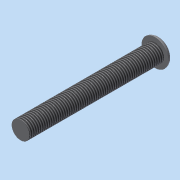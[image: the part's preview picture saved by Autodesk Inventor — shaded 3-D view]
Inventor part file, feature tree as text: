
AUTODESK INVENTOR PART (.ipt)
format: ipt  version: 2015 (Build 190159000, 159)  size: 94,208 bytes
history: native  units: mm
features: revolve x1, fillet x1, thread x1, sketch x1
ambient origin geometry x8: Origin, YZ Plane, XZ Plane, XY Plane, X Axis, Y Axis, Z Axis, Center Point
bodies: Solid1 (feature_tree)
feature tree (4):
  revolve  "Revolution1"  [1 undecoded]
  fillet  "Fillet1"  Radius=1.0mm
  thread  "Thread1"  [1 undecoded]
  sketch  "Sketch1"  dims[d0=2.0mm d1=3.0mm d2=1.0mm d3=90.0deg d4=1.0mm d5=10.0mm d6=0.0mm d7=30.0mm]
note: 2 required parameter values undecoded (feature->parameter linkage not recoverable at this tier; creation-order binding heuristic only, values carry confidence <= 0.55)